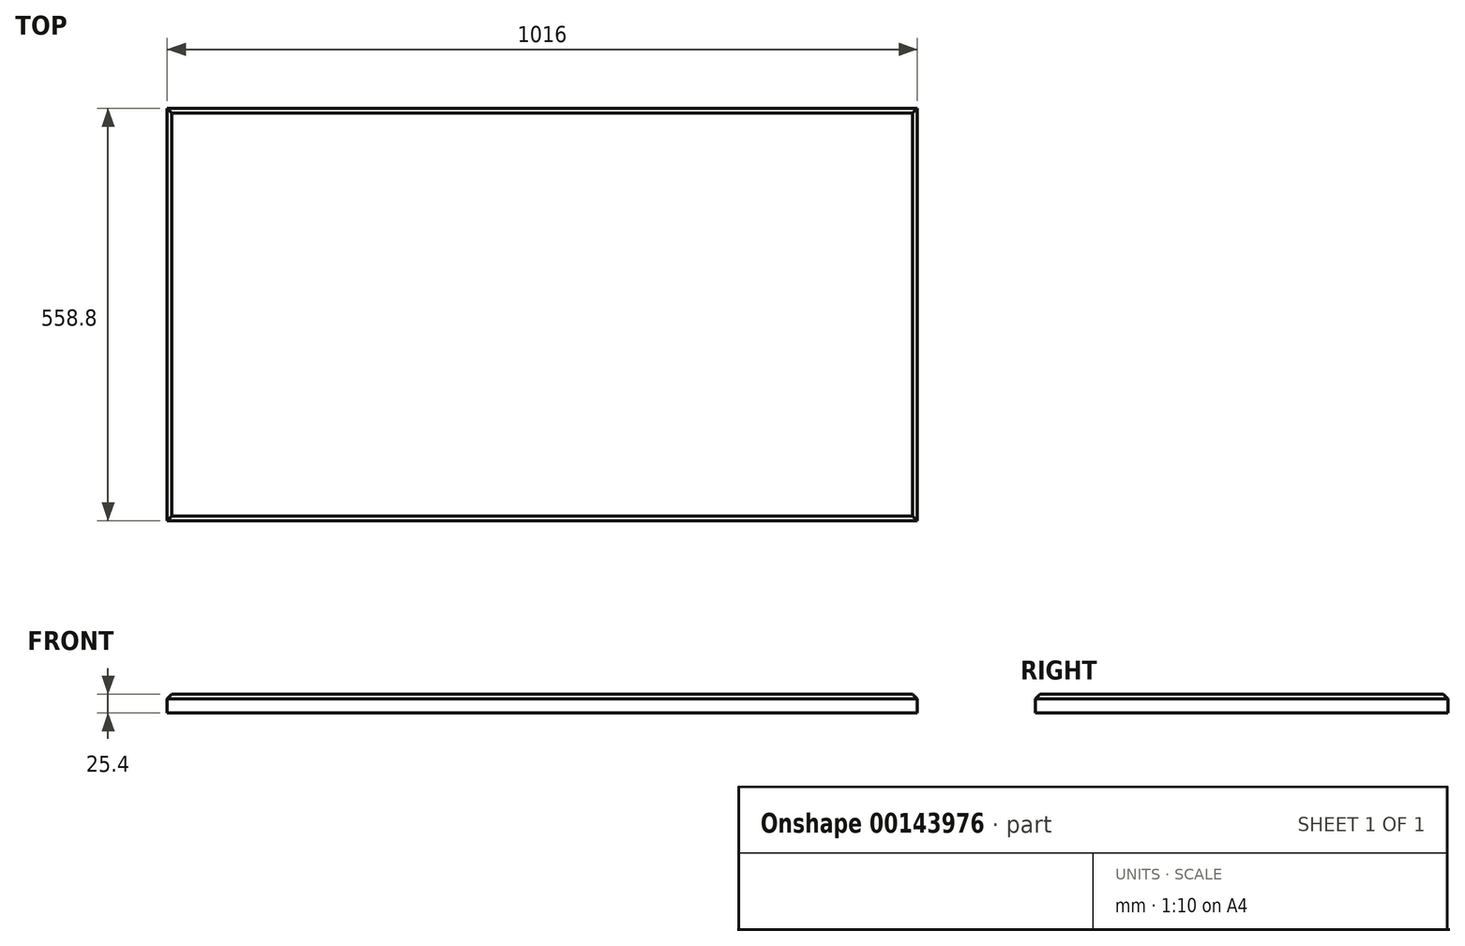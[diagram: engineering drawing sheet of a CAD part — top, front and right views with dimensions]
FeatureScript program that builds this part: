
annotation { "Feature Type Name" : "Feature", "Feature Type Description" : "" }
export const myFeature = defineFeature(function(context is Context, id is Id, definition is map)
    precondition{}
    {
        {
            var Q0;
            Q0=qCreatedBy(makeId("Top.planeOp"),FACE);
            var sketch = newSketch(context, id + "F0", { "sketchPlane" : qUnion([Q0])});
            skLineSegment(sketch, "E0.bottom", {"start": v(0, 0) * mm, "end": v(1016, 0) * mm});
            skLineSegment(sketch, "E0.top", {"start": v(0, 558.8) * mm, "end": v(1016, 558.8) * mm});
            skLineSegment(sketch, "E0.left", {"start": v(0, 0) * mm, "end": v(0, 558.8) * mm});
            skLineSegment(sketch, "E0.right", {"start": v(1016, 0) * mm, "end": v(1016, 558.8) * mm});
            skSolve(sketch);
        }
        {
            var Q0;
            Q0 = qSketchRegion(id + "F0", true);
            extrude(context, id + "F1", {"entities" : qUnion([Q0]), "depth" : 25.4 * mm});
        }
        {
            var Q0;
            Q0 = qSketchRegion(id + "F0", true);
            extrude(context, id + "F2", {"entities" : qUnion([Q0]), "operationType" : NewBodyOperationType.ADD, "depth" : 25.4 * mm});
        }
        {
            var Q0;
            Q0=makeQuery(id+"F1.opExtrude","CAP_EDGE",EDGE,{"disambiguationData":[OSD([sQuery(id+"F0.wireOp",EDGE,"E0.left")])],"isStart":false});
            var Q1;
            Q1=makeQuery(id+"F1.opExtrude","CAP_EDGE",EDGE,{"disambiguationData":[OSD([sQuery(id+"F0.wireOp",EDGE,"E0.bottom")])],"isStart":false});
            var Q2;
            Q2=makeQuery(id+"F1.opExtrude","CAP_EDGE",EDGE,{"disambiguationData":[OSD([sQuery(id+"F0.wireOp",EDGE,"E0.right")])],"isStart":false});
            var Q3;
            Q3=makeQuery(id+"F1.opExtrude","CAP_EDGE",EDGE,{"disambiguationData":[OSD([sQuery(id+"F0.wireOp",EDGE,"E0.top")])],"isStart":false});
            chamfer(context, id + "F3", {"entities" : qUnion([Q0, Q1, Q2, Q3]), "width" : 6.35 * mm, "tangentPropagation" : true});
        }
    });
